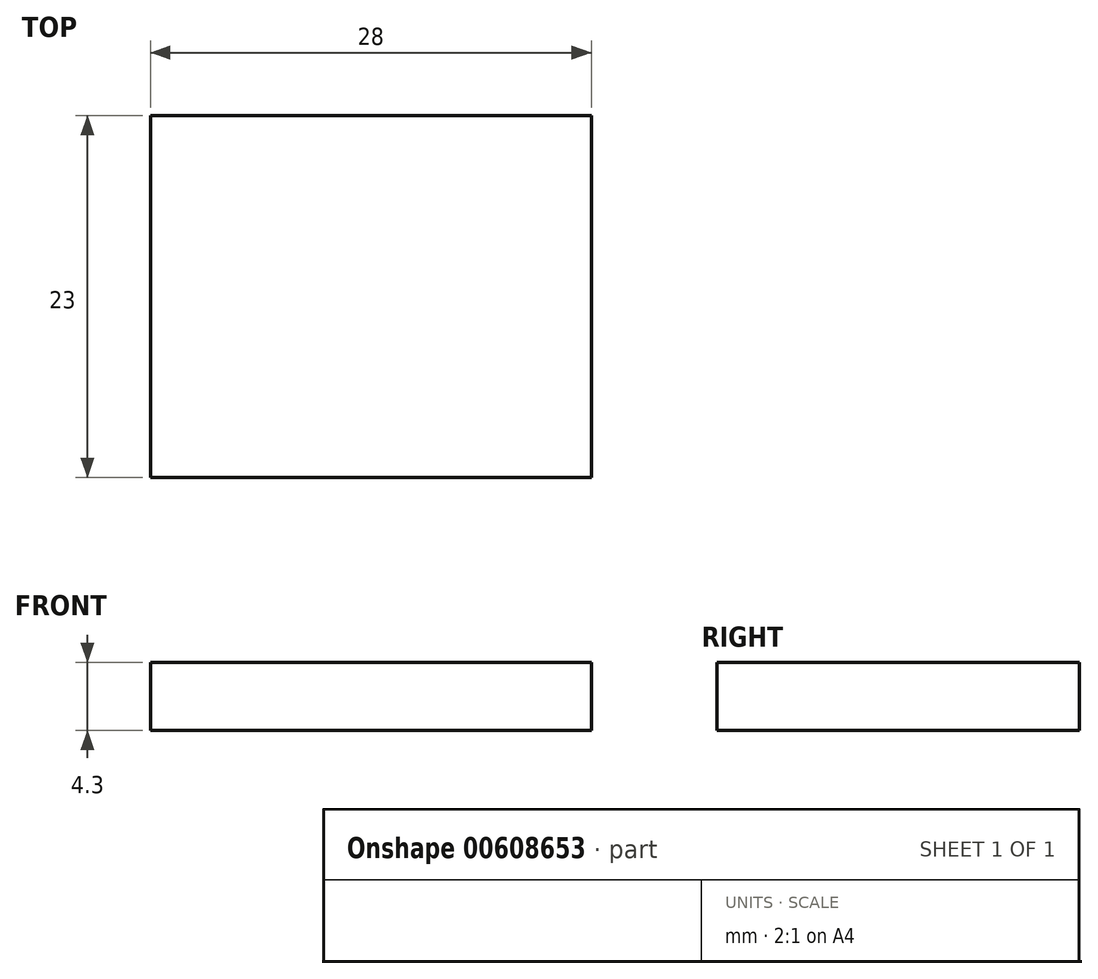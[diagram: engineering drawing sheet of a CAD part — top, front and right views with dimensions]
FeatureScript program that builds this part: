
annotation { "Feature Type Name" : "Feature", "Feature Type Description" : "" }
export const myFeature = defineFeature(function(context is Context, id is Id, definition is map)
    precondition{}
    {
        {
            var Q0;
            Q0=qCreatedBy(makeId("Top.planeOp"),FACE);
            var sketch = newSketch(context, id + "F0", { "sketchPlane" : qUnion([Q0])});
            skLineSegment(sketch, "E0.bottom", {"start": v(-21.06, 23) * mm, "end": v(6.94, 23) * mm});
            skLineSegment(sketch, "E0.top", {"start": v(-21.06, 0) * mm, "end": v(6.94, 0) * mm});
            skLineSegment(sketch, "E0.left", {"start": v(-21.06, 23) * mm, "end": v(-21.06, 0) * mm});
            skLineSegment(sketch, "E0.right", {"start": v(6.94, 23) * mm, "end": v(6.94, 0) * mm});
            skSolve(sketch);
        }
        {
            var Q0;
            Q0 = qSketchRegion(id + "F0", true);
            extrude(context, id + "F1", {"entities" : qUnion([Q0]), "depth" : 4.3 * mm, "offsetDistance" : 25 * mm});
        }
    });
